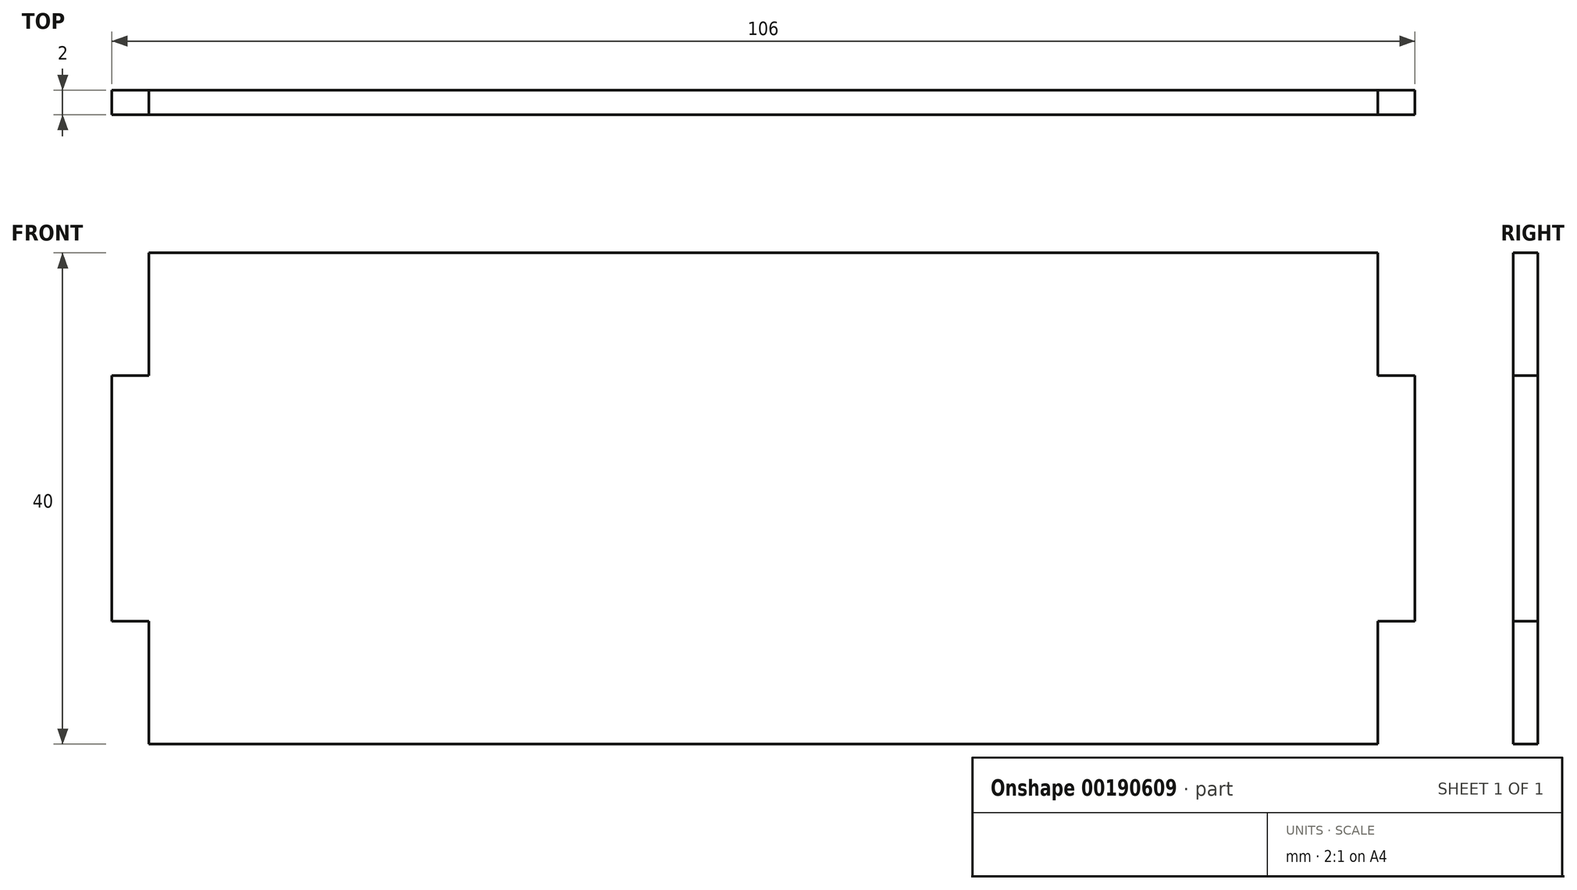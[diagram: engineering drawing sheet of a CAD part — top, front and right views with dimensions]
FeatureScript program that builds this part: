
annotation { "Feature Type Name" : "Feature", "Feature Type Description" : "" }
export const myFeature = defineFeature(function(context is Context, id is Id, definition is map)
    precondition{}
    {
        {
            var Q0;
            Q0=qCreatedBy(makeId("Front.planeOp"),FACE);
            var sketch = newSketch(context, id + "F0", { "sketchPlane" : qUnion([Q0])});
            skLineSegment(sketch, "E0.bottom", {"start": v(-50, 20) * mm, "end": v(50, 20) * mm});
            skLineSegment(sketch, "E0.top", {"start": v(-50, -20) * mm, "end": v(50, -20) * mm});
            skLineSegment(sketch, "E0.right", {"start": v(50, 20) * mm, "end": v(50, 10) * mm});
            skPoint(sketch, "E0.middle", {"position": v(0, 0) * mm});
            skLineSegment(sketch, "E1.bottom", {"start": v(50, 10) * mm, "end": v(53, 10) * mm});
            skLineSegment(sketch, "E1.top", {"start": v(50, -10) * mm, "end": v(53, -10) * mm});
            skLineSegment(sketch, "E1.right", {"start": v(53, 10) * mm, "end": v(53, -10) * mm});
            skLineSegment(sketch, "E2", {"start": v(0, 20) * mm, "end": v(0, -20) * mm, "construction": true});
            skLineSegment(sketch, "E3", {"start": v(50, -10) * mm, "end": v(50, -20) * mm});
            skLineSegment(sketch, "E4.MirrorCS", {"start": v(-50, -10) * mm, "end": v(-50, -20) * mm});
            skLineSegment(sketch, "E5.MirrorCS", {"start": v(-50, -10) * mm, "end": v(-53, -10) * mm});
            skLineSegment(sketch, "E6.MirrorCS", {"start": v(-53, 10) * mm, "end": v(-53, -10) * mm});
            skLineSegment(sketch, "E7.MirrorCS", {"start": v(-50, 10) * mm, "end": v(-53, 10) * mm});
            skLineSegment(sketch, "E8.MirrorCS", {"start": v(-50, 20) * mm, "end": v(-50, 10) * mm});
            skSolve(sketch);
        }
        {
            var Q0;
            Q0=makeQuery(id+"F0.imprint","IMPRINT",FACE,{"disambiguationData":[TD([[makeQuery(id+"F0.imprint","IMPRINT",EDGE,{"derivedFrom":sQuery(id+"F0.wireOp",EDGE,"E0.bottom")}),-1.0]])]});
            extrude(context, id + "F1", {"entities" : qUnion([Q0]), "depth" : 2 * mm});
        }
    });
